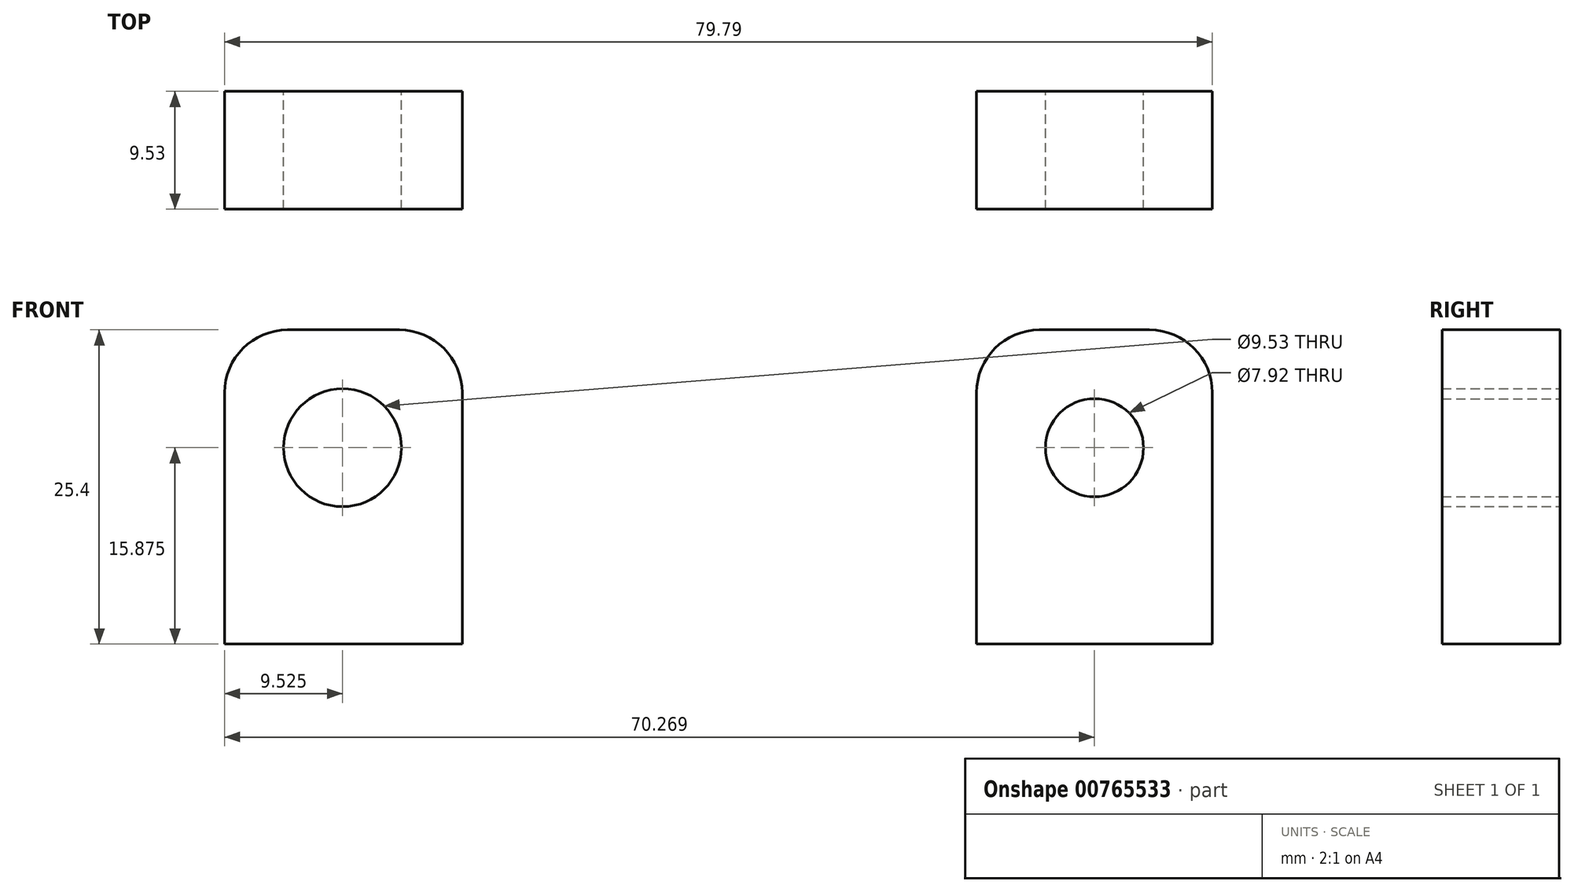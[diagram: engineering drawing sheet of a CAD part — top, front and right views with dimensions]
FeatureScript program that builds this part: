
annotation { "Feature Type Name" : "Feature", "Feature Type Description" : "" }
export const myFeature = defineFeature(function(context is Context, id is Id, definition is map)
    precondition{}
    {
        {
            var Q0;
            Q0=qCreatedBy(makeId("Front.planeOp"),FACE);
            var sketch = newSketch(context, id + "F0", { "sketchPlane" : qUnion([Q0])});
            skLineSegment(sketch, "E0.bottom", {"start": v(0, 0) * mm, "end": v(19.2, 0) * mm});
            skLineSegment(sketch, "E0.top", {"start": v(0, -25.4) * mm, "end": v(19.2, -25.4) * mm});
            skLineSegment(sketch, "E0.left", {"start": v(0, 0) * mm, "end": v(0, -25.4) * mm});
            skLineSegment(sketch, "E0.right", {"start": v(19.2, 0) * mm, "end": v(19.2, -25.4) * mm});
            skCircle(sketch, "E1", {"center": v(9.53, -9.53) * mm, "radius": 4.76 * mm});
            skLineSegment(sketch, "E2.bottom", {"start": v(60.74, 0) * mm, "end": v(79.8, 0) * mm});
            skLineSegment(sketch, "E2.top", {"start": v(60.74, -25.4) * mm, "end": v(79.8, -25.4) * mm});
            skLineSegment(sketch, "E2.left", {"start": v(60.74, 0) * mm, "end": v(60.74, -25.4) * mm});
            skLineSegment(sketch, "E2.right", {"start": v(79.8, 0) * mm, "end": v(79.8, -25.4) * mm});
            skCircle(sketch, "E3", {"center": v(70.27, -9.53) * mm, "radius": 3.96 * mm});
            skSolve(sketch);
        }
        {
            var Q0;
            Q0 = qSketchRegion(id + "F0", true);
            extrude(context, id + "F1", {"entities" : qUnion([Q0]), "depth" : 9.52 * mm, "offsetDistance" : 25.4 * mm});
        }
        {
            var Q0;
            Q0=makeQuery(id+"F1.opExtrude","CAP_FACE",FACE,{"disambiguationData":[OSD([sQuery(id+"F0.wireOp",EDGE,"E0.bottom"),sQuery(id+"F0.wireOp",EDGE,"E0.top"),sQuery(id+"F0.wireOp",EDGE,"E0.left"),sQuery(id+"F0.wireOp",EDGE,"E0.right"),sQuery(id+"F0.wireOp",EDGE,"E1")])],"isStart":true});
            extrude(context, id + "F2", {"entities" : qUnion([Q0]), "operationType" : NewBodyOperationType.ADD, "oppositeDirection" : true, "depth" : 9.52 * mm, "offsetDistance" : 25.4 * mm});
        }
        {
            var Q0;
            Q0=makeQuery(id+"F1.opExtrude","SWEPT_EDGE",EDGE,{"disambiguationData":[OSD([sQuery(id+"F0.wireOp",EDGE,"E2.bottom"),sQuery(id+"F0.wireOp",EDGE,"E2.left")])]});
            var Q1;
            Q1=makeQuery(id+"F1.opExtrude","SWEPT_EDGE",EDGE,{"disambiguationData":[OSD([sQuery(id+"F0.wireOp",EDGE,"E2.bottom"),sQuery(id+"F0.wireOp",EDGE,"E2.right")])]});
            fillet(context, id + "F3", {"entities" : qUnion([Q0, Q1]), "radius" : 5.08 * mm, "tangentPropagation" : true, "allowEdgeOverflow" : false});
        }
        {
            var Q0;
            Q0=makeQuery(id+"F1.opExtrude","SWEPT_EDGE",EDGE,{"disambiguationData":[OSD([sQuery(id+"F0.wireOp",EDGE,"E0.bottom"),sQuery(id+"F0.wireOp",EDGE,"E0.right")])]});
            var Q1;
            Q1=makeQuery(id+"F1.opExtrude","SWEPT_EDGE",EDGE,{"disambiguationData":[OSD([sQuery(id+"F0.wireOp",EDGE,"E0.bottom"),sQuery(id+"F0.wireOp",EDGE,"E0.left")])]});
            fillet(context, id + "F4", {"entities" : qUnion([Q0, Q1]), "radius" : 5.08 * mm, "tangentPropagation" : true, "allowEdgeOverflow" : false});
        }
    });
